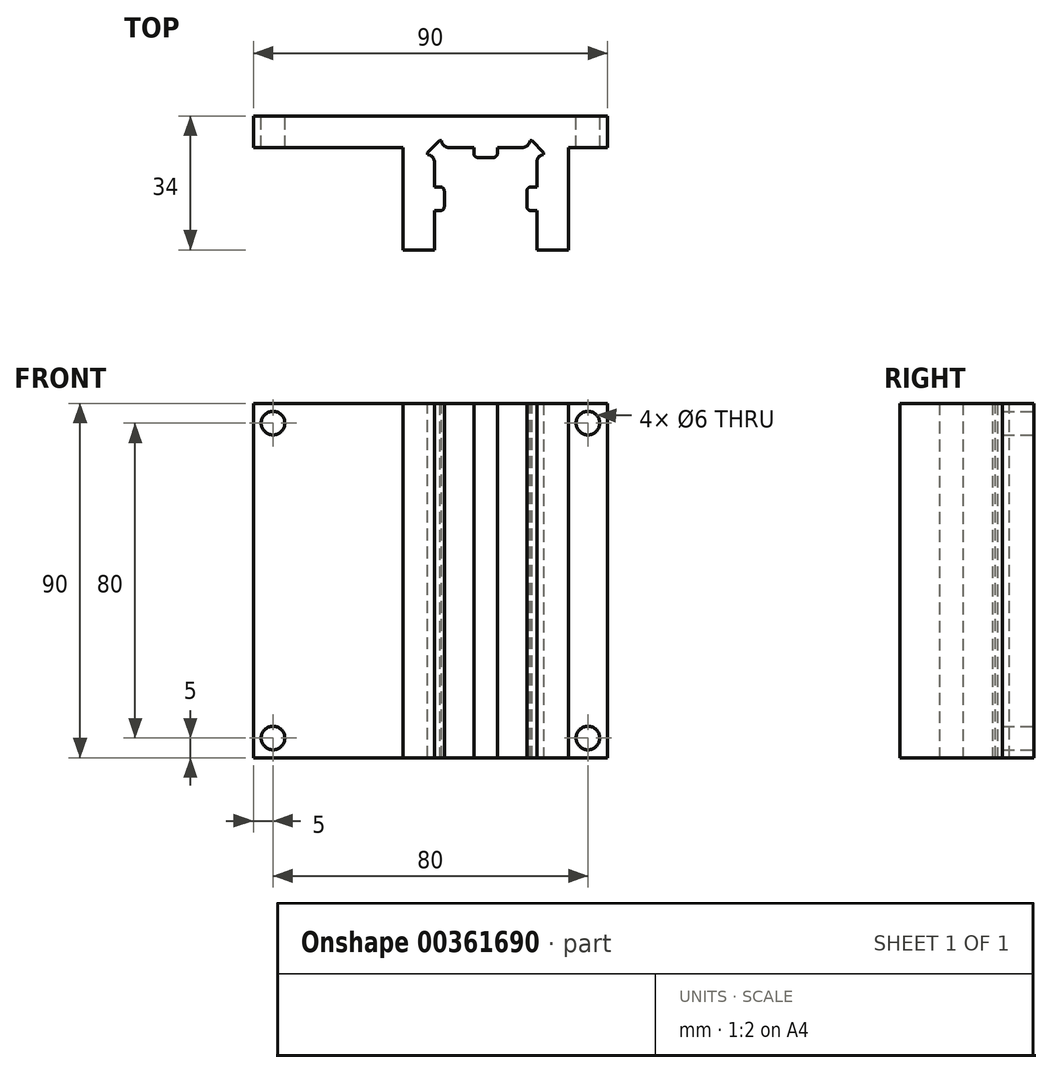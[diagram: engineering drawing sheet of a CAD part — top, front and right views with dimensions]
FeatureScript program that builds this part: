
annotation { "Feature Type Name" : "Feature", "Feature Type Description" : "" }
export const myFeature = defineFeature(function(context is Context, id is Id, definition is map)
    precondition{}
    {
        {
            var Q0;
            Q0=qCreatedBy(makeId("Top.planeOp"),FACE);
            var sketch = newSketch(context, id + "F0", { "sketchPlane" : qUnion([Q0])});
            skLineSegment(sketch, "E0", {"start": v(0, 0) * mm, "end": v(0, 26) * mm});
            skLineSegment(sketch, "E1", {"start": v(0, 26) * mm, "end": v(-38, 26) * mm});
            skLineSegment(sketch, "E2", {"start": v(-38, 26) * mm, "end": v(-38, 34) * mm});
            skLineSegment(sketch, "E3", {"start": v(-38, 34) * mm, "end": v(52, 34) * mm});
            skLineSegment(sketch, "E4", {"start": v(52, 34) * mm, "end": v(52, 26) * mm});
            skLineSegment(sketch, "E5", {"start": v(52, 26) * mm, "end": v(42, 26) * mm});
            skLineSegment(sketch, "E6", {"start": v(42, 26) * mm, "end": v(42, 0) * mm});
            skLineSegment(sketch, "E7", {"start": v(42, 0) * mm, "end": v(34, 0) * mm});
            skLineSegment(sketch, "E8", {"start": v(34, 0) * mm, "end": v(34, 10) * mm});
            skLineSegment(sketch, "E9", {"start": v(34, 10) * mm, "end": v(31.5, 10) * mm});
            skLineSegment(sketch, "E10", {"start": v(31.5, 10) * mm, "end": v(31.5, 16) * mm});
            skLineSegment(sketch, "E11", {"start": v(31.5, 16) * mm, "end": v(34, 16) * mm});
            skLineSegment(sketch, "E12", {"start": v(34, 16) * mm, "end": v(34, 26) * mm});
            skLineSegment(sketch, "E13", {"start": v(34, 26) * mm, "end": v(24, 26) * mm});
            skLineSegment(sketch, "E14", {"start": v(24, 26) * mm, "end": v(24, 23.5) * mm});
            skLineSegment(sketch, "E15", {"start": v(24, 23.5) * mm, "end": v(18, 23.5) * mm});
            skLineSegment(sketch, "E16", {"start": v(18, 23.5) * mm, "end": v(18, 26) * mm});
            skLineSegment(sketch, "E17", {"start": v(18, 26) * mm, "end": v(8, 26) * mm});
            skLineSegment(sketch, "E18", {"start": v(8, 26) * mm, "end": v(8, 16) * mm});
            skLineSegment(sketch, "E19", {"start": v(8, 16) * mm, "end": v(10.5, 16) * mm});
            skLineSegment(sketch, "E20", {"start": v(10.5, 16) * mm, "end": v(10.5, 10) * mm});
            skLineSegment(sketch, "E21", {"start": v(10.5, 10) * mm, "end": v(8, 10) * mm});
            skLineSegment(sketch, "E22", {"start": v(8, 10) * mm, "end": v(8, 0) * mm});
            skLineSegment(sketch, "E23", {"start": v(8, 0) * mm, "end": v(0, 0) * mm});
            skSolve(sketch);
        }
        {
            var Q0;
            Q0=makeQuery(id+"F0.imprint","IMPRINT",FACE,{"disambiguationData":[TD([[makeQuery(id+"F0.imprint","IMPRINT",EDGE,{"derivedFrom":sQuery(id+"F0.wireOp",EDGE,"E0")}),-1.0]])]});
            extrude(context, id + "F1", {"entities" : qUnion([Q0]), "depth" : 90 * mm});
        }
        {
            var Q0;
            Q0=makeQuery(id+"F1.opExtrude","SWEPT_FACE",FACE,{"disambiguationData":[OSD([sQuery(id+"F0.wireOp",EDGE,"E3")])]});
            var sketch = newSketch(context, id + "F2", { "sketchPlane" : qUnion([Q0])});
            skLineSegment(sketch, "E24", {"start": v(-52, 85) * mm, "end": v(38, 85) * mm, "construction": true});
            skLineSegment(sketch, "E25", {"start": v(33, 90) * mm, "end": v(33, 0) * mm, "construction": true});
            skLineSegment(sketch, "E26", {"start": v(-47, 90) * mm, "end": v(-47, 0) * mm, "construction": true});
            skLineSegment(sketch, "E27", {"start": v(-52, 5) * mm, "end": v(38, 5) * mm, "construction": true});
            skCircle(sketch, "E28", {"center": v(33, 85) * mm, "radius": 3 * mm});
            skCircle(sketch, "E29", {"center": v(33, 5) * mm, "radius": 3 * mm});
            skCircle(sketch, "E30", {"center": v(-47, 5) * mm, "radius": 3 * mm});
            skCircle(sketch, "E31", {"center": v(-47, 85) * mm, "radius": 3 * mm});
            skSolve(sketch);
        }
        {
            var Q0;
            Q0 = qSketchRegion(id + "F2", true);
            extrude(context, id + "F3", {"entities" : qUnion([Q0]), "operationType" : NewBodyOperationType.REMOVE, "oppositeDirection" : true, "depth" : 25 * mm});
        }
        {
            var Q0;
            Q0=makeQuery(id+"F1.opExtrude","CAP_FACE",FACE,{"disambiguationData":[OSD([sQuery(id+"F0.wireOp",EDGE,"E0"),sQuery(id+"F0.wireOp",EDGE,"E1"),sQuery(id+"F0.wireOp",EDGE,"E2"),sQuery(id+"F0.wireOp",EDGE,"E3"),sQuery(id+"F0.wireOp",EDGE,"E4"),sQuery(id+"F0.wireOp",EDGE,"E5"),sQuery(id+"F0.wireOp",EDGE,"E6"),sQuery(id+"F0.wireOp",EDGE,"E7"),sQuery(id+"F0.wireOp",EDGE,"E8"),sQuery(id+"F0.wireOp",EDGE,"E9"),sQuery(id+"F0.wireOp",EDGE,"E10"),sQuery(id+"F0.wireOp",EDGE,"E11"),sQuery(id+"F0.wireOp",EDGE,"E12"),sQuery(id+"F0.wireOp",EDGE,"E13"),sQuery(id+"F0.wireOp",EDGE,"E14"),sQuery(id+"F0.wireOp",EDGE,"E15"),sQuery(id+"F0.wireOp",EDGE,"E16"),sQuery(id+"F0.wireOp",EDGE,"E17"),sQuery(id+"F0.wireOp",EDGE,"E18"),sQuery(id+"F0.wireOp",EDGE,"E19"),sQuery(id+"F0.wireOp",EDGE,"E20"),sQuery(id+"F0.wireOp",EDGE,"E21"),sQuery(id+"F0.wireOp",EDGE,"E22"),sQuery(id+"F0.wireOp",EDGE,"E23")])],"isStart":false});
            var sketch = newSketch(context, id + "F4", { "sketchPlane" : qUnion([Q0])});
            skLineSegment(sketch, "E32.bottom", {"start": v(6.25, 24.25) * mm, "end": v(9.75, 24.25) * mm});
            skLineSegment(sketch, "E32.top", {"start": v(6.25, 27.75) * mm, "end": v(9.75, 27.75) * mm});
            skLineSegment(sketch, "E32.left", {"start": v(6.25, 24.25) * mm, "end": v(6.25, 27.75) * mm});
            skLineSegment(sketch, "E32.right", {"start": v(9.75, 24.25) * mm, "end": v(9.75, 27.75) * mm});
            skPoint(sketch, "E32.middle", {"position": v(8, 26) * mm});
            skLineSegment(sketch, "E33.bottom", {"start": v(35.75, 24.25) * mm, "end": v(32.25, 24.25) * mm});
            skLineSegment(sketch, "E33.top", {"start": v(35.75, 27.75) * mm, "end": v(32.25, 27.75) * mm});
            skLineSegment(sketch, "E33.left", {"start": v(35.75, 24.25) * mm, "end": v(35.75, 27.75) * mm});
            skLineSegment(sketch, "E33.right", {"start": v(32.25, 24.25) * mm, "end": v(32.25, 27.75) * mm});
            skPoint(sketch, "E33.middle", {"position": v(34, 26) * mm});
            skSolve(sketch);
        }
        {
            var Q0;
            Q0 = qSketchRegion(id + "F4", true);
            extrude(context, id + "F5", {"entities" : qUnion([Q0]), "operationType" : NewBodyOperationType.REMOVE, "oppositeDirection" : true, "depth" : 300 * mm});
        }
        {
            var Q0;
            Q0=makeQuery(id+"F5.boolean.opBoolean","COPY",EDGE,{"derivedFrom":makeQuery(id+"F5.opExtrude","SWEPT_EDGE",EDGE,{"disambiguationData":[OSD([sQuery(id+"F4.wireOp",EDGE,"E32.top"),sQuery(id+"F4.wireOp",EDGE,"E32.left")])]})});
            chamfer(context, id + "F6", {"entities" : qUnion([Q0]), "width" : 3 * mm, "tangentPropagation" : true});
        }
        {
            var Q0;
            Q0=makeQuery(id+"F5.boolean.opBoolean","COPY",EDGE,{"derivedFrom":makeQuery(id+"F5.opExtrude","SWEPT_EDGE",EDGE,{"disambiguationData":[OSD([sQuery(id+"F4.wireOp",EDGE,"E33.top"),sQuery(id+"F4.wireOp",EDGE,"E33.left")])]})});
            chamfer(context, id + "F7", {"entities" : qUnion([Q0]), "width" : 3 * mm, "tangentPropagation" : true});
        }
        {
            var Q0;
            Q0=makeQuery(id+"F1.opExtrude","SWEPT_EDGE",EDGE,{"disambiguationData":[OSD([sQuery(id+"F0.wireOp",EDGE,"E20"),sQuery(id+"F0.wireOp",EDGE,"E21")])]});
            var Q1;
            Q1=makeQuery(id+"F1.opExtrude","SWEPT_EDGE",EDGE,{"disambiguationData":[OSD([sQuery(id+"F0.wireOp",EDGE,"E19"),sQuery(id+"F0.wireOp",EDGE,"E20")])]});
            var Q2;
            Q2=makeQuery(id+"F1.opExtrude","SWEPT_EDGE",EDGE,{"disambiguationData":[OSD([sQuery(id+"F0.wireOp",EDGE,"E15"),sQuery(id+"F0.wireOp",EDGE,"E16")])]});
            var Q3;
            Q3=makeQuery(id+"F1.opExtrude","SWEPT_EDGE",EDGE,{"disambiguationData":[OSD([sQuery(id+"F0.wireOp",EDGE,"E14"),sQuery(id+"F0.wireOp",EDGE,"E15")])]});
            var Q4;
            Q4=makeQuery(id+"F1.opExtrude","SWEPT_EDGE",EDGE,{"disambiguationData":[OSD([sQuery(id+"F0.wireOp",EDGE,"E9"),sQuery(id+"F0.wireOp",EDGE,"E10")])]});
            var Q5;
            Q5=makeQuery(id+"F1.opExtrude","SWEPT_EDGE",EDGE,{"disambiguationData":[OSD([sQuery(id+"F0.wireOp",EDGE,"E10"),sQuery(id+"F0.wireOp",EDGE,"E11")])]});
            fillet(context, id + "F8", {"entities" : qUnion([Q0, Q1, Q2, Q3, Q4, Q5]), "radius" : 1 * mm, "tangentPropagation" : true, "allowEdgeOverflow" : false});
        }
        {
            var Q0;
            Q0=makeQuery(id+"F5.boolean.opBoolean","INTERSECT",EDGE,{"derivedFrom":[makeQuery(id+"F1.opExtrude","SWEPT_FACE",FACE,{"disambiguationData":[OSD([sQuery(id+"F0.wireOp",EDGE,"E12")])]}),makeQuery(id+"F5.opExtrude","SWEPT_FACE",FACE,{"disambiguationData":[OSD([sQuery(id+"F4.wireOp",EDGE,"E33.bottom")])]})]});
            var Q1;
            Q1=makeQuery(id+"F5.boolean.opBoolean","INTERSECT",EDGE,{"derivedFrom":[makeQuery(id+"F1.opExtrude","SWEPT_FACE",FACE,{"disambiguationData":[OSD([sQuery(id+"F0.wireOp",EDGE,"E13")])]}),makeQuery(id+"F5.opExtrude","SWEPT_FACE",FACE,{"disambiguationData":[OSD([sQuery(id+"F4.wireOp",EDGE,"E33.right")])]})]});
            fillet(context, id + "F9", {"entities" : qUnion([Q0, Q1]), "radius" : 2 * mm, "tangentPropagation" : true, "allowEdgeOverflow" : false});
        }
        {
            var Q0;
            Q0=makeQuery(id+"F5.boolean.opBoolean","INTERSECT",EDGE,{"derivedFrom":[makeQuery(id+"F1.opExtrude","SWEPT_FACE",FACE,{"disambiguationData":[OSD([sQuery(id+"F0.wireOp",EDGE,"E17")])]}),makeQuery(id+"F5.opExtrude","SWEPT_FACE",FACE,{"disambiguationData":[OSD([sQuery(id+"F4.wireOp",EDGE,"E32.right")])]})]});
            var Q1;
            Q1=makeQuery(id+"F5.boolean.opBoolean","INTERSECT",EDGE,{"derivedFrom":[makeQuery(id+"F1.opExtrude","SWEPT_FACE",FACE,{"disambiguationData":[OSD([sQuery(id+"F0.wireOp",EDGE,"E18")])]}),makeQuery(id+"F5.opExtrude","SWEPT_FACE",FACE,{"disambiguationData":[OSD([sQuery(id+"F4.wireOp",EDGE,"E32.bottom")])]})]});
            fillet(context, id + "F10", {"entities" : qUnion([Q0, Q1]), "radius" : 2 * mm, "tangentPropagation" : true, "allowEdgeOverflow" : false});
        }
    });
